# Revit family: Basic_Valves-Full_Port-WATTS-LFF116_4in_Globe_150
name_source: partatom
category: Pipe Accessories
revit_build: Autodesk Revit 2016 (Build: 20150714_1515(x64)
units: mm (PartAtom-declared; Revit-internal decimal feet)

## family parameters
Always vertical = Yes
Cut with Voids When Loaded = No
OmniClass Number = 23.65.55.14
OmniClass Title = Valves for Liquid Services
Part Type = Valve - Breaks Into
Round Connector Dimension = Use Radius
Shared = Yes
Work Plane-Based = No

## types (1)
- LFF116 - 4" (Globe 150#)
    Body Radius = 2 1/2"
    Center to Top = 8 5/8"
    Connection Radius = 2"
    Connection Size = 4"
    Connection Type = 150#
    Country = United States
    Description = The Watts ACV Models F100 and F1100 are single chamber basic valves that incorporate a one-piece disc and diaphragm assembly. This assembly is the only moving part within the valve allowing it to open, close or modulate as commanded by the pilot control system. Model F100 is a globe pattern design. Model F1100 is an angle pattern design.
    Flange Geometry = Yes
    Flange Radius = 3 1/2"
    Flange Thickness = 1/2"
    Inlet Connection = 4" Inlet Connection
    Inner Length = 7"
    Lenght 2 = 15"
    Manufacturer = WATTS
    Manufacturer Product Line = Automatic Control Valves
    Material = Metal-WATTS-Ductile Iron
    Model = F100
    NPT Port Size K = 1/2"
    NPT Port Size K radius = 1/8"
    NPT Port Size M = 3/8"
    Nominal Dist. = 3/4"
    Nominal Height = 2 7/8"
    Nominal Radius 1 = 3/8"
    Nominal Radius 2  ( L ) = 1/2"
    Nominal Thickness = 3/4"
    Nominal Width = 4 1/2"
    Outlet Connection = 4" Outlet Connection
    Overall Length = 15"
    Pressure Rating = 250.00 psi
    Price = Prices may vary. Please consult Manufacturer Representative for most up-to-date price list.
    Product Documentation Link = http://media.wattswater.com
    Product Page URL = https://www.watts.com
    Region = North America
    URL = http://www.watts.com
    Warranty Information = 1 Year (Limited)
    Weight = 190 lbs. 86 kgs.

## geometry (parser evidence)
native form markers: Sweep x4
no freeform markers — native parametric forms only
